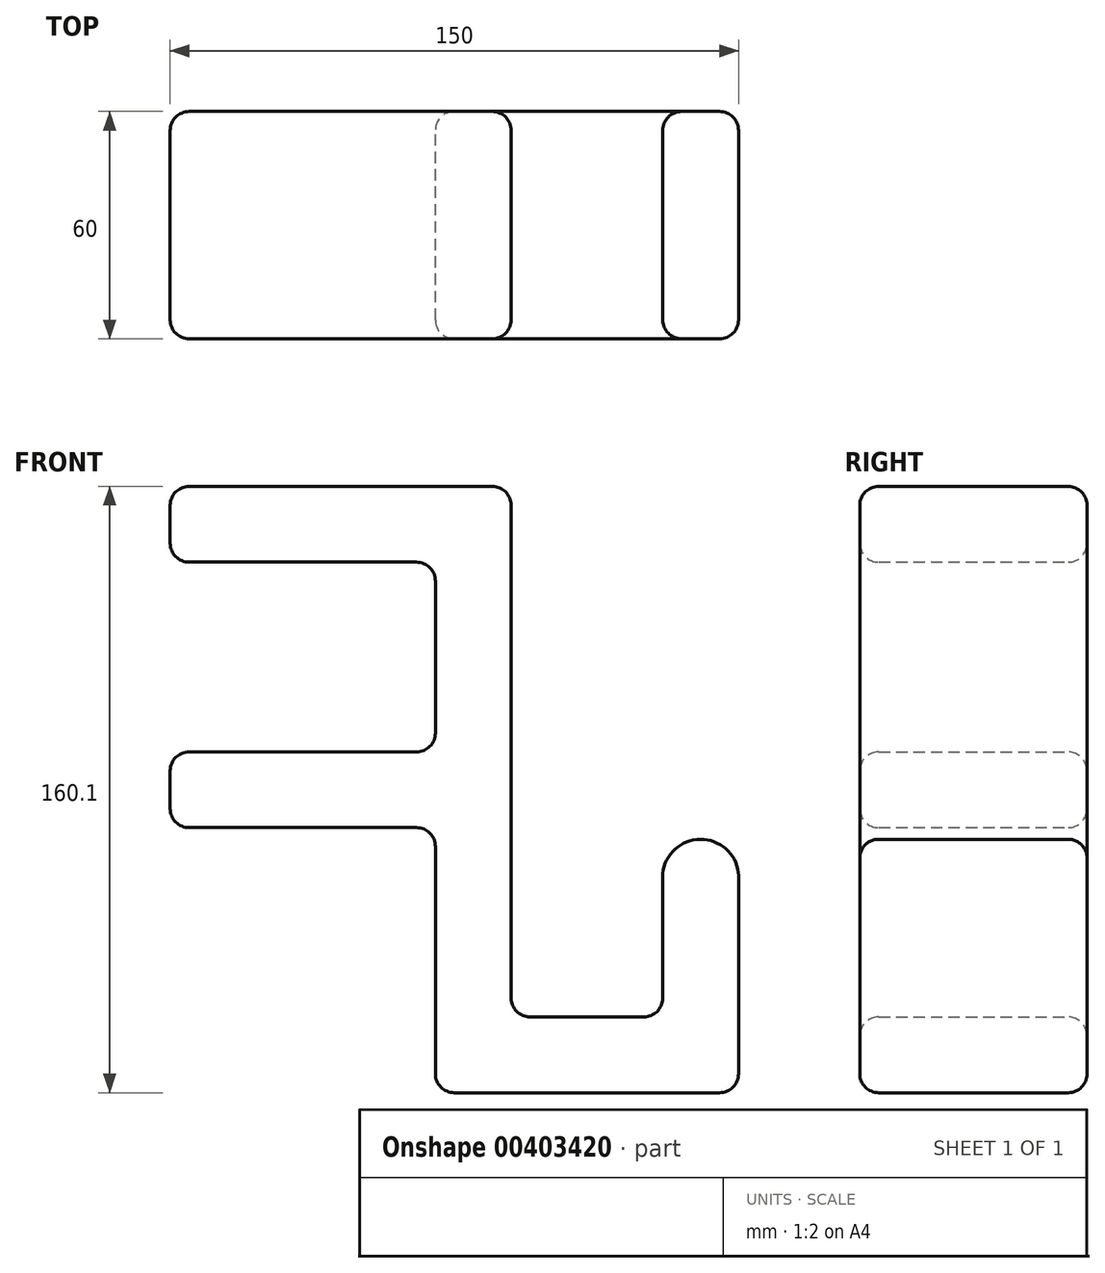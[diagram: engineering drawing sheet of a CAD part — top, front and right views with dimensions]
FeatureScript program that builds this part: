
annotation { "Feature Type Name" : "Feature", "Feature Type Description" : "" }
export const myFeature = defineFeature(function(context is Context, id is Id, definition is map)
    precondition{}
    {
        {
            var Q0;
            Q0=qCreatedBy(makeId("Front.planeOp"),FACE);
            var sketch = newSketch(context, id + "F0", { "sketchPlane" : qUnion([Q0])});
            skLineSegment(sketch, "E0", {"start": v(0, 78.11) * mm, "end": v(-70, 78.11) * mm});
            skLineSegment(sketch, "E1", {"start": v(-70, 78.11) * mm, "end": v(-70, 58.11) * mm});
            skLineSegment(sketch, "E2", {"start": v(-70, 58.11) * mm, "end": v(0, 58.11) * mm});
            skLineSegment(sketch, "E3", {"start": v(0, 58.11) * mm, "end": v(0, 8.01) * mm});
            skLineSegment(sketch, "E4", {"start": v(0, 8.01) * mm, "end": v(-70, 8.01) * mm});
            skLineSegment(sketch, "E5", {"start": v(-70, 8.01) * mm, "end": v(-70, -11.99) * mm});
            skLineSegment(sketch, "E6", {"start": v(-70, -11.99) * mm, "end": v(0, -11.99) * mm});
            skLineSegment(sketch, "E7", {"start": v(0, -11.99) * mm, "end": v(0, -81.99) * mm});
            skLineSegment(sketch, "E8", {"start": v(0, -81.99) * mm, "end": v(80, -81.99) * mm});
            skLineSegment(sketch, "E9", {"start": v(80, -81.99) * mm, "end": v(80, -11.99) * mm});
            skLineSegment(sketch, "E10", {"start": v(80, -11.99) * mm, "end": v(60, -11.99) * mm});
            skLineSegment(sketch, "E11", {"start": v(60, -11.99) * mm, "end": v(60, -61.99) * mm});
            skLineSegment(sketch, "E12", {"start": v(60, -61.99) * mm, "end": v(20, -61.99) * mm});
            skLineSegment(sketch, "E13", {"start": v(20, -61.99) * mm, "end": v(20, 78.11) * mm});
            skLineSegment(sketch, "E14", {"start": v(20, 78.11) * mm, "end": v(0, 78.11) * mm});
            skSolve(sketch);
        }
        {
            var Q0;
            Q0 = qSketchRegion(id + "F0", true);
            extrude(context, id + "F1", {"entities" : qUnion([Q0]), "endBound" : BoundingType.SYMMETRIC, "depth" : 60 * mm});
        }
        {
            var Q0;
            Q0=makeQuery(id+"F1.opExtrude","CAP_FACE",FACE,{"disambiguationData":[OSD([sQuery(id+"F0.wireOp",EDGE,"E0"),sQuery(id+"F0.wireOp",EDGE,"E1"),sQuery(id+"F0.wireOp",EDGE,"E2"),sQuery(id+"F0.wireOp",EDGE,"E3"),sQuery(id+"F0.wireOp",EDGE,"E4"),sQuery(id+"F0.wireOp",EDGE,"E5"),sQuery(id+"F0.wireOp",EDGE,"E6"),sQuery(id+"F0.wireOp",EDGE,"E7"),sQuery(id+"F0.wireOp",EDGE,"E8"),sQuery(id+"F0.wireOp",EDGE,"E9"),sQuery(id+"F0.wireOp",EDGE,"E10"),sQuery(id+"F0.wireOp",EDGE,"E11"),sQuery(id+"F0.wireOp",EDGE,"E12"),sQuery(id+"F0.wireOp",EDGE,"E13"),sQuery(id+"F0.wireOp",EDGE,"E14")])],"isStart":false});
            var sketch = newSketch(context, id + "F2", { "sketchPlane" : qUnion([Q0])});
            skArc(sketch, "E15", {"start": v(80, -24.25) * mm, "mid": v(69.94, -15.06) * mm, "end": v(60, -24.39) * mm});
            skSolve(sketch);
        }
        {
            var Q0;
            Q0 = qSketchRegion(id + "F2", true);
            var Q1;
            {var subQ0=sQuery(id+"F2.wireOp",EDGE,"E15");Q1=makeQuery(id+"F2.imprint","IMPRINT",FACE,{"disambiguationData":[TD([[makeQuery(id+"F2.imprint","IMPRINT",EDGE,{"derivedFrom":subQ0}),-1.0]])]});}
            extrude(context, id + "F3", {"entities" : qUnion([Q0, Q1]), "operationType" : NewBodyOperationType.REMOVE, "oppositeDirection" : true, "depth" : 75.1 * mm});
        }
        {
            var Q0;
            Q0=makeQuery(id+"F3.boolean.opBoolean","COPY",EDGE,{"derivedFrom":makeQuery(id+"F3.opExtrude","CAP_EDGE",EDGE,{"disambiguationData":[OSD([sQuery(id+"F2.wireOp",EDGE,"E15")])],"isStart":true})});
            var Q1;
            Q1=makeQuery(id+"F1.opExtrude","SWEPT_FACE",FACE,{"disambiguationData":[OSD([sQuery(id+"F0.wireOp",EDGE,"E0"),sQuery(id+"F0.wireOp",EDGE,"E14")])]});
            var Q2;
            Q2=makeQuery(id+"F1.opExtrude","CAP_FACE",FACE,{"disambiguationData":[OSD([sQuery(id+"F0.wireOp",EDGE,"E0"),sQuery(id+"F0.wireOp",EDGE,"E1"),sQuery(id+"F0.wireOp",EDGE,"E2"),sQuery(id+"F0.wireOp",EDGE,"E3"),sQuery(id+"F0.wireOp",EDGE,"E4"),sQuery(id+"F0.wireOp",EDGE,"E5"),sQuery(id+"F0.wireOp",EDGE,"E6"),sQuery(id+"F0.wireOp",EDGE,"E7"),sQuery(id+"F0.wireOp",EDGE,"E8"),sQuery(id+"F0.wireOp",EDGE,"E9"),sQuery(id+"F0.wireOp",EDGE,"E10"),sQuery(id+"F0.wireOp",EDGE,"E11"),sQuery(id+"F0.wireOp",EDGE,"E12"),sQuery(id+"F0.wireOp",EDGE,"E13"),sQuery(id+"F0.wireOp",EDGE,"E14")])],"isStart":false});
            var Q3;
            Q3=makeQuery(id+"F1.opExtrude","SWEPT_FACE",FACE,{"disambiguationData":[OSD([sQuery(id+"F0.wireOp",EDGE,"E13")])]});
            var Q4;
            Q4=makeQuery(id+"F1.opExtrude","SWEPT_FACE",FACE,{"disambiguationData":[OSD([sQuery(id+"F0.wireOp",EDGE,"E8")])]});
            var Q5;
            Q5=makeQuery(id+"F1.opExtrude","SWEPT_FACE",FACE,{"disambiguationData":[OSD([sQuery(id+"F0.wireOp",EDGE,"E7")])]});
            var Q6;
            Q6=makeQuery(id+"F1.opExtrude","SWEPT_FACE",FACE,{"disambiguationData":[OSD([sQuery(id+"F0.wireOp",EDGE,"E6")])]});
            var Q7;
            Q7=makeQuery(id+"F1.opExtrude","SWEPT_FACE",FACE,{"disambiguationData":[OSD([sQuery(id+"F0.wireOp",EDGE,"E1")])]});
            var Q8;
            Q8=makeQuery(id+"F3.boolean.opBoolean","COPY",FACE,{"derivedFrom":makeQuery(id+"F3.opExtrude","SWEPT_FACE",FACE,{"disambiguationData":[OSD([sQuery(id+"F2.wireOp",EDGE,"E15")])]})});
            var Q9;
            Q9=makeQuery(id+"F1.opExtrude","SWEPT_EDGE",EDGE,{"disambiguationData":[OSD([sQuery(id+"F0.wireOp",EDGE,"E5"),sQuery(id+"F0.wireOp",EDGE,"E6")])]});
            var Q10;
            Q10=makeQuery(id+"F1.opExtrude","CAP_EDGE",EDGE,{"disambiguationData":[OSD([sQuery(id+"F0.wireOp",EDGE,"E11")])],"isStart":false});
            var Q11;
            Q11=makeQuery(id+"F1.opExtrude","SWEPT_FACE",FACE,{"disambiguationData":[OSD([sQuery(id+"F0.wireOp",EDGE,"E2")])]});
            var Q12;
            Q12=makeQuery(id+"F1.opExtrude","SWEPT_FACE",FACE,{"disambiguationData":[OSD([sQuery(id+"F0.wireOp",EDGE,"E3")])]});
            var Q13;
            Q13=makeQuery(id+"F1.opExtrude","SWEPT_FACE",FACE,{"disambiguationData":[OSD([sQuery(id+"F0.wireOp",EDGE,"E4")])]});
            var Q14;
            Q14=makeQuery(id+"F1.opExtrude","SWEPT_EDGE",EDGE,{"disambiguationData":[OSD([sQuery(id+"F0.wireOp",EDGE,"E8"),sQuery(id+"F0.wireOp",EDGE,"E9")])]});
            var Q15;
            Q15=makeQuery(id+"F1.opExtrude","SWEPT_EDGE",EDGE,{"disambiguationData":[OSD([sQuery(id+"F0.wireOp",EDGE,"E7"),sQuery(id+"F0.wireOp",EDGE,"E8")])]});
            var Q16;
            Q16=makeQuery(id+"F1.opExtrude","SWEPT_FACE",FACE,{"disambiguationData":[OSD([sQuery(id+"F0.wireOp",EDGE,"E12")])]});
            var Q17;
            Q17=makeQuery(id+"F1.opExtrude","CAP_FACE",FACE,{"disambiguationData":[OSD([sQuery(id+"F0.wireOp",EDGE,"E0"),sQuery(id+"F0.wireOp",EDGE,"E1"),sQuery(id+"F0.wireOp",EDGE,"E2"),sQuery(id+"F0.wireOp",EDGE,"E3"),sQuery(id+"F0.wireOp",EDGE,"E4"),sQuery(id+"F0.wireOp",EDGE,"E5"),sQuery(id+"F0.wireOp",EDGE,"E6"),sQuery(id+"F0.wireOp",EDGE,"E7"),sQuery(id+"F0.wireOp",EDGE,"E8"),sQuery(id+"F0.wireOp",EDGE,"E9"),sQuery(id+"F0.wireOp",EDGE,"E10"),sQuery(id+"F0.wireOp",EDGE,"E11"),sQuery(id+"F0.wireOp",EDGE,"E12"),sQuery(id+"F0.wireOp",EDGE,"E13"),sQuery(id+"F0.wireOp",EDGE,"E14")])],"isStart":true});
            var Q18;
            Q18=makeQuery(id+"F1.opExtrude","SWEPT_FACE",FACE,{"disambiguationData":[OSD([sQuery(id+"F0.wireOp",EDGE,"E9")])]});
            var Q19;
            Q19=makeQuery(id+"F1.opExtrude","SWEPT_EDGE",EDGE,{"disambiguationData":[OSD([sQuery(id+"F0.wireOp",EDGE,"E13"),sQuery(id+"F0.wireOp",EDGE,"E14")])]});
            var Q20;
            Q20=makeQuery(id+"F1.opExtrude","CAP_EDGE",EDGE,{"disambiguationData":[OSD([sQuery(id+"F0.wireOp",EDGE,"E12")])],"isStart":true});
            var Q21;
            Q21=makeQuery(id+"F1.opExtrude","CAP_EDGE",EDGE,{"disambiguationData":[OSD([sQuery(id+"F0.wireOp",EDGE,"E9")])],"isStart":true});
            var Q22;
            Q22=makeQuery(id+"F1.opExtrude","CAP_EDGE",EDGE,{"disambiguationData":[OSD([sQuery(id+"F0.wireOp",EDGE,"E8")])],"isStart":true});
            var Q23;
            Q23=makeQuery(id+"F3.boolean.opBoolean","INTERSECT",EDGE,{"derivedFrom":[makeQuery(id+"F1.opExtrude","CAP_FACE",FACE,{"disambiguationData":[OSD([sQuery(id+"F0.wireOp",EDGE,"E0"),sQuery(id+"F0.wireOp",EDGE,"E1"),sQuery(id+"F0.wireOp",EDGE,"E2"),sQuery(id+"F0.wireOp",EDGE,"E3"),sQuery(id+"F0.wireOp",EDGE,"E4"),sQuery(id+"F0.wireOp",EDGE,"E5"),sQuery(id+"F0.wireOp",EDGE,"E6"),sQuery(id+"F0.wireOp",EDGE,"E7"),sQuery(id+"F0.wireOp",EDGE,"E8"),sQuery(id+"F0.wireOp",EDGE,"E9"),sQuery(id+"F0.wireOp",EDGE,"E10"),sQuery(id+"F0.wireOp",EDGE,"E11"),sQuery(id+"F0.wireOp",EDGE,"E12"),sQuery(id+"F0.wireOp",EDGE,"E13"),sQuery(id+"F0.wireOp",EDGE,"E14")])],"isStart":true}),makeQuery(id+"F3.opExtrude","SWEPT_FACE",FACE,{"disambiguationData":[OSD([sQuery(id+"F2.wireOp",EDGE,"E15")])]})]});
            var Q24;
            Q24=makeQuery(id+"F1.opExtrude","CAP_EDGE",EDGE,{"disambiguationData":[OSD([sQuery(id+"F0.wireOp",EDGE,"E12")])],"isStart":false});
            var Q25;
            Q25=makeQuery(id+"F1.opExtrude","SWEPT_EDGE",EDGE,{"disambiguationData":[OSD([sQuery(id+"F0.wireOp",EDGE,"E2"),sQuery(id+"F0.wireOp",EDGE,"E3")])]});
            var Q26;
            Q26=makeQuery(id+"F1.opExtrude","CAP_EDGE",EDGE,{"disambiguationData":[OSD([sQuery(id+"F0.wireOp",EDGE,"E13")])],"isStart":false});
            var Q27;
            Q27=makeQuery(id+"F1.opExtrude","SWEPT_EDGE",EDGE,{"disambiguationData":[OSD([sQuery(id+"F0.wireOp",EDGE,"E1"),sQuery(id+"F0.wireOp",EDGE,"E2")])]});
            var Q28;
            Q28=makeQuery(id+"F1.opExtrude","CAP_EDGE",EDGE,{"disambiguationData":[OSD([sQuery(id+"F0.wireOp",EDGE,"E9")])],"isStart":false});
            var Q29;
            Q29=makeQuery(id+"F1.opExtrude","CAP_EDGE",EDGE,{"disambiguationData":[OSD([sQuery(id+"F0.wireOp",EDGE,"E13")])],"isStart":true});
            var Q30;
            Q30=makeQuery(id+"F1.opExtrude","CAP_EDGE",EDGE,{"disambiguationData":[OSD([sQuery(id+"F0.wireOp",EDGE,"E4")])],"isStart":false});
            var Q31;
            Q31=makeQuery(id+"F1.opExtrude","CAP_EDGE",EDGE,{"disambiguationData":[OSD([sQuery(id+"F0.wireOp",EDGE,"E1")])],"isStart":false});
            var Q32;
            Q32=makeQuery(id+"F3.boolean.opBoolean","COPY",EDGE,{"derivedFrom":makeQuery(id+"F3.opExtrude","SWEPT_EDGE",EDGE,{"disambiguationData":[OSD([sQuery(id+"F0.wireOp",EDGE,"E11"),sQuery(id+"F2.wireOp",EDGE,"E15")])]})});
            var Q33;
            Q33=makeQuery(id+"F1.opExtrude","CAP_EDGE",EDGE,{"disambiguationData":[OSD([sQuery(id+"F0.wireOp",EDGE,"E3")])],"isStart":true});
            var Q34;
            Q34=makeQuery(id+"F1.opExtrude","CAP_EDGE",EDGE,{"disambiguationData":[OSD([sQuery(id+"F0.wireOp",EDGE,"E2")])],"isStart":false});
            var Q35;
            Q35=makeQuery(id+"F1.opExtrude","CAP_EDGE",EDGE,{"disambiguationData":[OSD([sQuery(id+"F0.wireOp",EDGE,"E0"),sQuery(id+"F0.wireOp",EDGE,"E14")])],"isStart":false});
            var Q36;
            Q36=makeQuery(id+"F1.opExtrude","CAP_EDGE",EDGE,{"disambiguationData":[OSD([sQuery(id+"F0.wireOp",EDGE,"E3")])],"isStart":false});
            var Q37;
            Q37=makeQuery(id+"F1.opExtrude","CAP_EDGE",EDGE,{"disambiguationData":[OSD([sQuery(id+"F0.wireOp",EDGE,"E6")])],"isStart":false});
            var Q38;
            Q38=makeQuery(id+"F3.boolean.opBoolean","COPY",EDGE,{"derivedFrom":makeQuery(id+"F3.opExtrude","SWEPT_EDGE",EDGE,{"disambiguationData":[OSD([sQuery(id+"F0.wireOp",EDGE,"E9"),sQuery(id+"F2.wireOp",EDGE,"E15")])]})});
            var Q39;
            Q39=makeQuery(id+"F1.opExtrude","CAP_EDGE",EDGE,{"disambiguationData":[OSD([sQuery(id+"F0.wireOp",EDGE,"E11")])],"isStart":true});
            var Q40;
            Q40=makeQuery(id+"F1.opExtrude","CAP_EDGE",EDGE,{"disambiguationData":[OSD([sQuery(id+"F0.wireOp",EDGE,"E7")])],"isStart":true});
            var Q41;
            Q41=makeQuery(id+"F1.opExtrude","CAP_EDGE",EDGE,{"disambiguationData":[OSD([sQuery(id+"F0.wireOp",EDGE,"E8")])],"isStart":false});
            var Q42;
            Q42=makeQuery(id+"F1.opExtrude","SWEPT_EDGE",EDGE,{"disambiguationData":[OSD([sQuery(id+"F0.wireOp",EDGE,"E3"),sQuery(id+"F0.wireOp",EDGE,"E4")])]});
            var Q43;
            Q43=makeQuery(id+"F1.opExtrude","CAP_EDGE",EDGE,{"disambiguationData":[OSD([sQuery(id+"F0.wireOp",EDGE,"E2")])],"isStart":true});
            var Q44;
            Q44=makeQuery(id+"F1.opExtrude","CAP_EDGE",EDGE,{"disambiguationData":[OSD([sQuery(id+"F0.wireOp",EDGE,"E7")])],"isStart":false});
            var Q45;
            Q45=makeQuery(id+"F1.opExtrude","SWEPT_EDGE",EDGE,{"disambiguationData":[OSD([sQuery(id+"F0.wireOp",EDGE,"E12"),sQuery(id+"F0.wireOp",EDGE,"E13")])]});
            var Q46;
            Q46=makeQuery(id+"F1.opExtrude","CAP_EDGE",EDGE,{"disambiguationData":[OSD([sQuery(id+"F0.wireOp",EDGE,"E6")])],"isStart":true});
            var Q47;
            Q47=makeQuery(id+"F1.opExtrude","CAP_EDGE",EDGE,{"disambiguationData":[OSD([sQuery(id+"F0.wireOp",EDGE,"E1")])],"isStart":true});
            var Q48;
            Q48=makeQuery(id+"F1.opExtrude","SWEPT_EDGE",EDGE,{"disambiguationData":[OSD([sQuery(id+"F0.wireOp",EDGE,"E4"),sQuery(id+"F0.wireOp",EDGE,"E5")])]});
            var Q49;
            Q49=makeQuery(id+"F1.opExtrude","SWEPT_EDGE",EDGE,{"disambiguationData":[OSD([sQuery(id+"F0.wireOp",EDGE,"E0"),sQuery(id+"F0.wireOp",EDGE,"E1")])]});
            var Q50;
            Q50=makeQuery(id+"F1.opExtrude","SWEPT_EDGE",EDGE,{"disambiguationData":[OSD([sQuery(id+"F0.wireOp",EDGE,"E11"),sQuery(id+"F0.wireOp",EDGE,"E12")])]});
            var Q51;
            Q51=makeQuery(id+"F1.opExtrude","SWEPT_EDGE",EDGE,{"disambiguationData":[OSD([sQuery(id+"F0.wireOp",EDGE,"E6"),sQuery(id+"F0.wireOp",EDGE,"E7")])]});
            var Q52;
            Q52=makeQuery(id+"F1.opExtrude","SWEPT_FACE",FACE,{"disambiguationData":[OSD([sQuery(id+"F0.wireOp",EDGE,"E11")])]});
            var Q53;
            Q53=makeQuery(id+"F1.opExtrude","SWEPT_FACE",FACE,{"disambiguationData":[OSD([sQuery(id+"F0.wireOp",EDGE,"E5")])]});
            var Q54;
            Q54=makeQuery(id+"F1.opExtrude","CAP_EDGE",EDGE,{"disambiguationData":[OSD([sQuery(id+"F0.wireOp",EDGE,"E0"),sQuery(id+"F0.wireOp",EDGE,"E14")])],"isStart":true});
            var Q55;
            Q55=makeQuery(id+"F1.opExtrude","CAP_EDGE",EDGE,{"disambiguationData":[OSD([sQuery(id+"F0.wireOp",EDGE,"E4")])],"isStart":true});
            var Q56;
            Q56=makeQuery(id+"F1.opExtrude","CAP_EDGE",EDGE,{"disambiguationData":[OSD([sQuery(id+"F0.wireOp",EDGE,"E5")])],"isStart":false});
            var Q57;
            Q57=makeQuery(id+"F1.opExtrude","CAP_EDGE",EDGE,{"disambiguationData":[OSD([sQuery(id+"F0.wireOp",EDGE,"E5")])],"isStart":true});
            fillet(context, id + "F4", {"entities" : qUnion([Q0, Q1, Q2, Q3, Q4, Q5, Q6, Q7, Q8, Q9, Q10, Q11, Q12, Q13, Q14, Q15, Q16, Q17, Q18, Q19, Q20, Q21, Q22, Q23, Q24, Q25, Q26, Q27, Q28, Q29, Q30, Q31, Q32, Q33, Q34, Q35, Q36, Q37, Q38, Q39, Q40, Q41, Q42, Q43, Q44, Q45, Q46, Q47, Q48, Q49, Q50, Q51, Q52, Q53, Q54, Q55, Q56, Q57]), "radius" : 5 * mm, "tangentPropagation" : true, "allowEdgeOverflow" : false});
        }
    });
